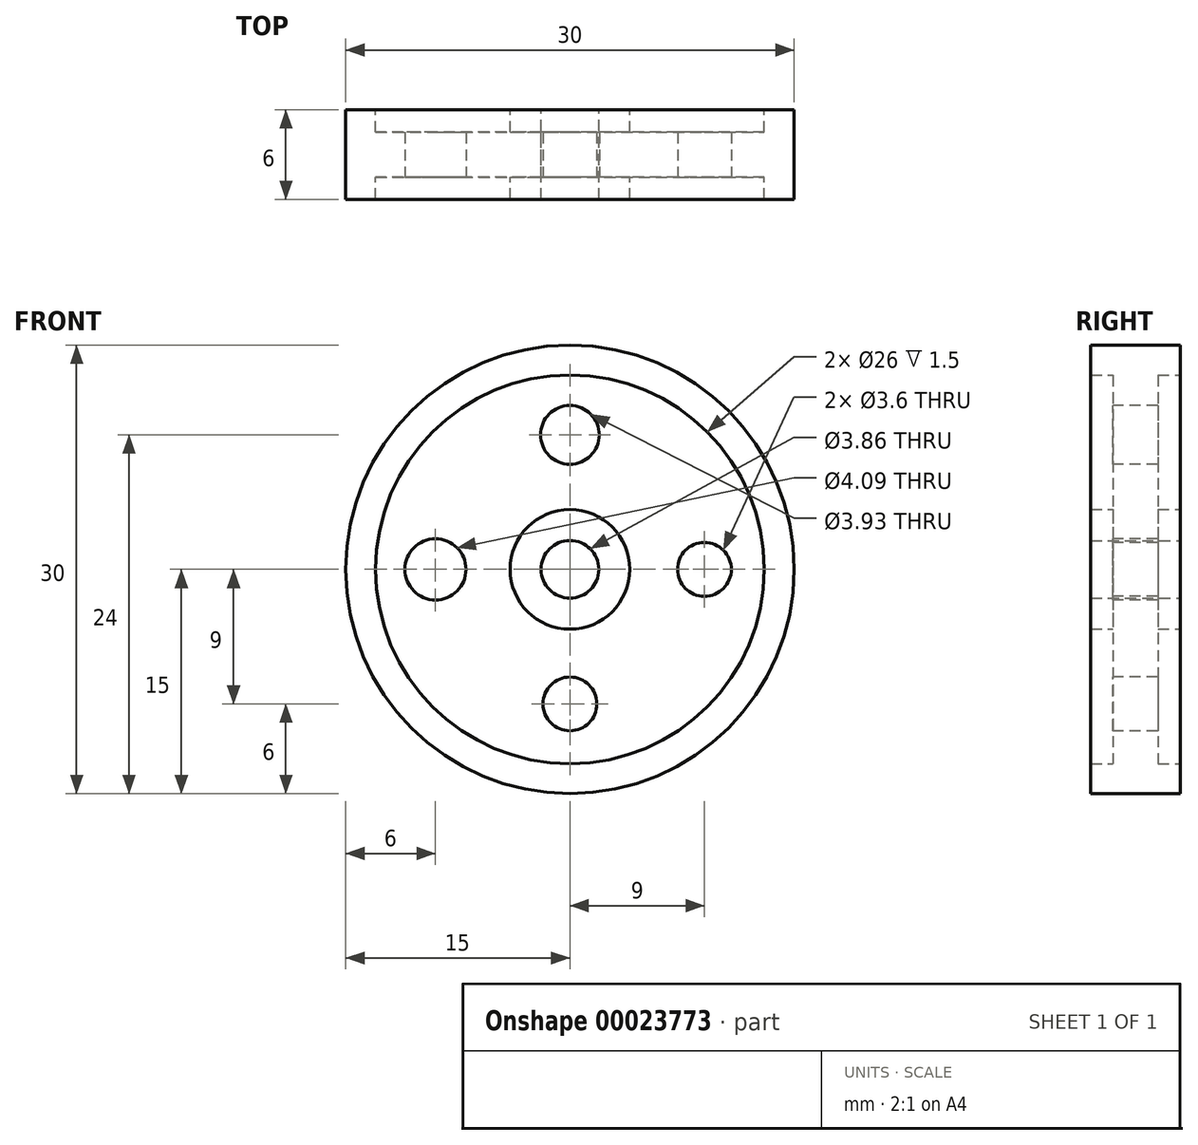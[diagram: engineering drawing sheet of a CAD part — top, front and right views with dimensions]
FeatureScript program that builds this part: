
annotation { "Feature Type Name" : "Feature", "Feature Type Description" : "" }
export const myFeature = defineFeature(function(context is Context, id is Id, definition is map)
    precondition{}
    {
        {
            var Q0;
            Q0=qCreatedBy(makeId("Right.planeOp"),FACE);
            var sketch = newSketch(context, id + "F0", { "sketchPlane" : qUnion([Q0])});
            skLineSegment(sketch, "E0", {"start": v(0, 0) * mm, "end": v(-10.79, 0) * mm, "construction": true});
            skLineSegment(sketch, "E1.bottom", {"start": v(2.86, 1.93) * mm, "end": v(-3.14, 1.93) * mm});
            skLineSegment(sketch, "E1.top", {"start": v(2.86, 4) * mm, "end": v(-3.14, 4) * mm});
            skLineSegment(sketch, "E1.left", {"start": v(2.86, 1.93) * mm, "end": v(2.86, 4) * mm});
            skLineSegment(sketch, "E1.right", {"start": v(-3.14, 1.93) * mm, "end": v(-3.14, 4) * mm});
            skLineSegment(sketch, "E2.bottom", {"start": v(1.36, 4) * mm, "end": v(-1.64, 4) * mm});
            skLineSegment(sketch, "E2.left", {"start": v(1.36, 4) * mm, "end": v(1.36, 13) * mm});
            skLineSegment(sketch, "E2.right", {"start": v(-1.64, 4) * mm, "end": v(-1.64, 13) * mm});
            skLineSegment(sketch, "E3.bottom", {"start": v(2.86, 13) * mm, "end": v(1.36, 13) * mm});
            skLineSegment(sketch, "E3.top", {"start": v(2.86, 15) * mm, "end": v(-3.14, 15) * mm});
            skLineSegment(sketch, "E3.left", {"start": v(2.86, 13) * mm, "end": v(2.86, 15) * mm});
            skLineSegment(sketch, "E3.right", {"start": v(-3.14, 13) * mm, "end": v(-3.14, 15) * mm});
            skLineSegment(sketch, "E4.trimOffspring", {"start": v(-1.64, 13) * mm, "end": v(-3.14, 13) * mm});
            skSolve(sketch);
        }
        {
            var Q0;
            Q0 = qSketchRegion(id + "F0", true);
            var Q1;
            Q1=sQuery(id+"F0.wireOp",EDGE,"E0");
            revolve(context, id + "F1", {"entities" : qUnion([Q0]), "axis" : qUnion([Q1]), "revolveType" : RevolveType.FULL});
        }
        {
            var Q0;
            Q0=makeQuery(id+"F1.opRevolve","SWEPT_FACE",FACE,{"disambiguationData":[OSD([sQuery(id+"F0.wireOp",EDGE,"E2.right")])]});
            var sketch = newSketch(context, id + "F2", { "sketchPlane" : qUnion([Q0])});
            skCircle(sketch, "E5", {"center": v(0, 9) * mm, "radius": 1.97 * mm});
            skCircle(sketch, "E6", {"center": v(9, 0) * mm, "radius": 1.8 * mm});
            skCircle(sketch, "E7", {"center": v(0, -9) * mm, "radius": 1.8 * mm});
            skCircle(sketch, "E8", {"center": v(-9, 0) * mm, "radius": 2.04 * mm});
            skSolve(sketch);
        }
        {
            var Q0;
            Q0 = qSketchRegion(id + "F2", true);
            extrude(context, id + "F3", {"entities" : qUnion([Q0]), "operationType" : NewBodyOperationType.REMOVE, "endBound" : BoundingType.THROUGH_ALL, "oppositeDirection" : true, "depth" : 25 * mm});
        }
    });
